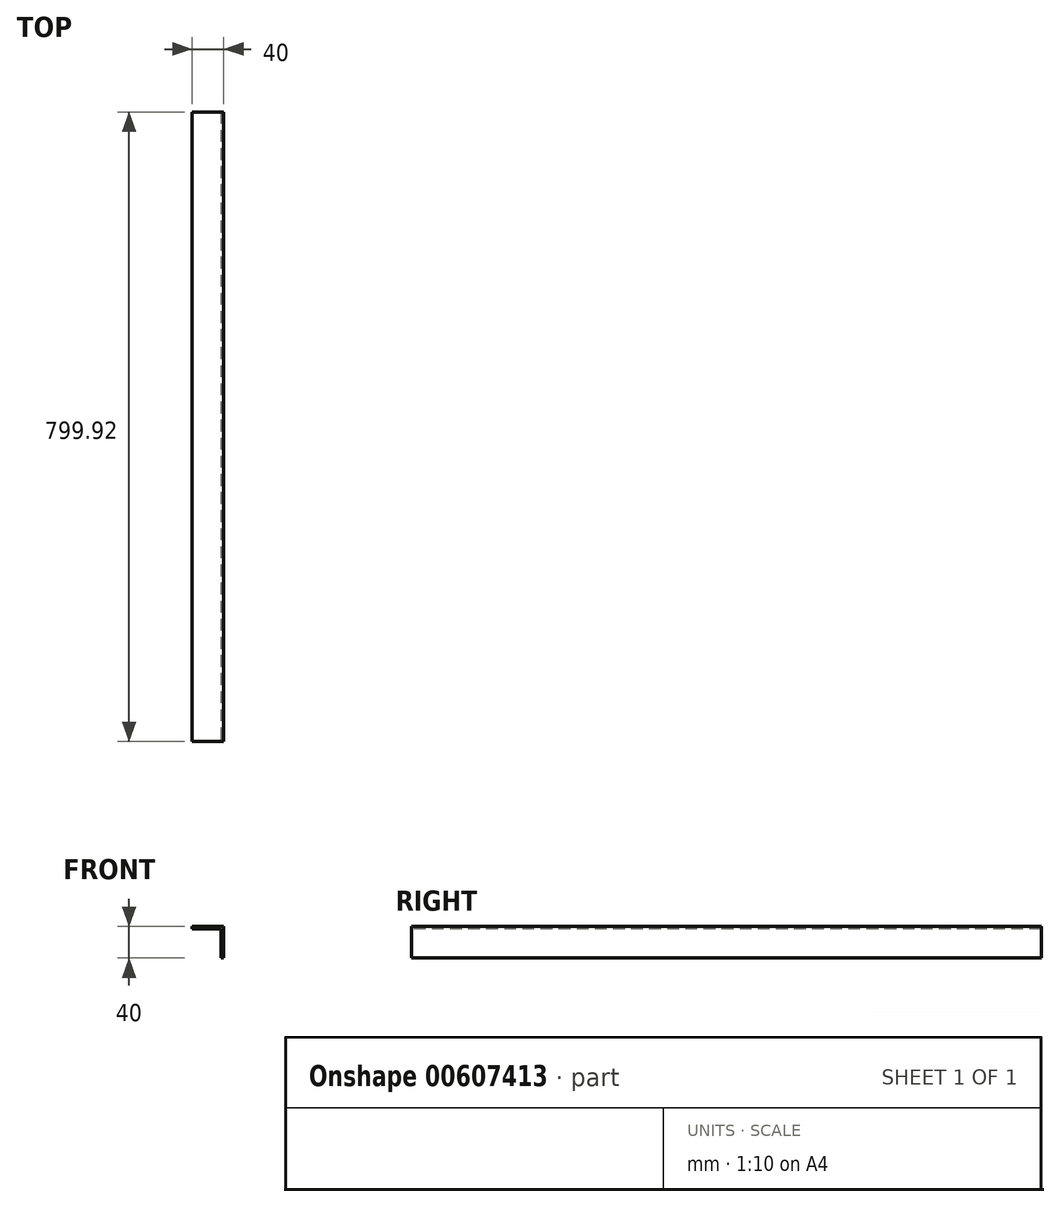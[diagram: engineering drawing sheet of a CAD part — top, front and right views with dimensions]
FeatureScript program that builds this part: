
annotation { "Feature Type Name" : "Feature", "Feature Type Description" : "" }
export const myFeature = defineFeature(function(context is Context, id is Id, definition is map)
    precondition{}
    {
        {
            var Q0;
            Q0=qCreatedBy(makeId("Top.planeOp"),FACE);
            var sketch = newSketch(context, id + "F0", { "sketchPlane" : qUnion([Q0])});
            skLineSegment(sketch, "E0.right", {"start": v(0, 399.96) * mm, "end": v(0, -399.96) * mm});
            skSolve(sketch);
        }
        {
            var Q0;
            Q0=qCreatedBy(makeId("Front.planeOp"),FACE);
            var sketch = newSketch(context, id + "F1", { "sketchPlane" : qUnion([Q0])});
            skLineSegment(sketch, "E1", {"start": v(20, 0) * mm, "end": v(-20, 0) * mm});
            skLineSegment(sketch, "E2", {"start": v(-20, 0) * mm, "end": v(20, 0) * mm});
            skLineSegment(sketch, "E3", {"start": v(20, -40) * mm, "end": v(20, 0) * mm});
            skLineSegment(sketch, "E4.0", {"start": v(16.83, -40) * mm, "end": v(16.83, -3.17) * mm});
            skLineSegment(sketch, "E4.1", {"start": v(-20, -3.18) * mm, "end": v(16.83, -3.17) * mm});
            skLineSegment(sketch, "E5", {"start": v(-20, 0) * mm, "end": v(-20, -3.18) * mm});
            skLineSegment(sketch, "E6", {"start": v(16.83, -40) * mm, "end": v(20, -40) * mm});
            skPoint(sketch, "E7", {"position": v(0, 0) * mm});
            skSolve(sketch);
        }
        {
            var Q0;
            Q0 = qSketchRegion(id + "F1", true);
            var Q1;
            Q1 = qConstructionFilter(qBodyType(qCreatedBy(id + "F0" ,EDGE), BodyType.WIRE), ConstructionObject.NO);
            sweep(context, id + "F2", {"profiles" : qUnion([Q0]), "path" : qUnion([Q1]), "keepProfileOrientation" : true});
        }
    });
